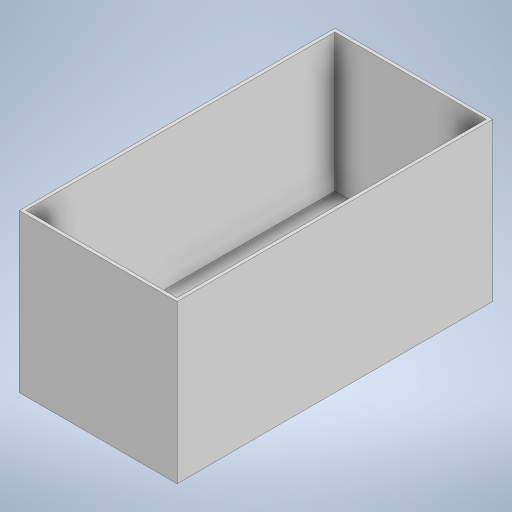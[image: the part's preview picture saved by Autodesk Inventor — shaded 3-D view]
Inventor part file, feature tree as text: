
AUTODESK INVENTOR PART (.ipt)
format: ipt  version: 2024 (Build 280153000, 153)  size: 200,192 bytes
history: native  units: in
note: dims shown in document units (in); Inventor stores cm internally (conversion verified against a paired STEP export)
features: extrude x3, sketch x3
ambient origin geometry x8: Origin, YZ Plane, XZ Plane, XY Plane, X Axis, Y Axis, Z Axis, Center Point
bodies: Solid1 (feature_tree)
feature tree (6):
  extrude  "Extrusion1"  Depth=24.0in
  extrude  "Extrusion2"  Depth=0.25in
  extrude  "Extrusion3"  Depth=0.25in
  sketch  "Sketch1"  dims[d0=12.0in d1=24.0in]
  sketch  "Sketch2"  dims[d2=12.0in d3=0.0in d4=0.25in]
  sketch  "Sketch3"  dims[d5=0.25in d6=0.25in d7=0.25in d8=10.5in d9=0.0in d10=0.25in d11=0.25in d12=1.25in d13=0.0in]
